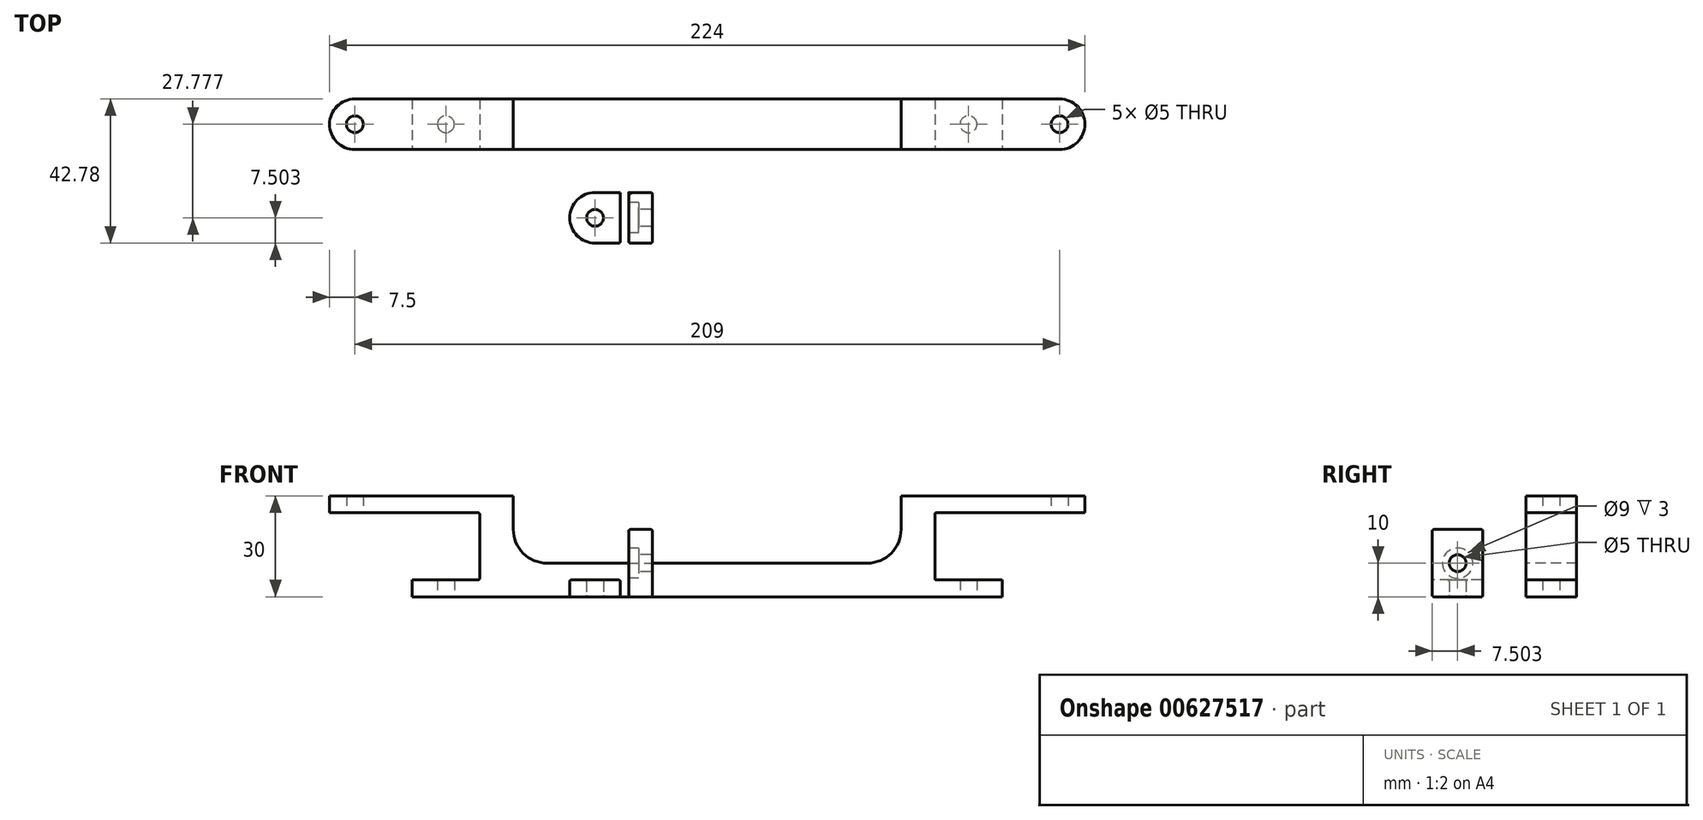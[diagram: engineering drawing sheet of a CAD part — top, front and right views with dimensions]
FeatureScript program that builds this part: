
annotation { "Feature Type Name" : "Feature", "Feature Type Description" : "" }
export const myFeature = defineFeature(function(context is Context, id is Id, definition is map)
    precondition{}
    {
        {
            var Q0;
            Q0=qCreatedBy(makeId("Top.planeOp"),FACE);
            var sketch = newSketch(context, id + "F0", { "sketchPlane" : qUnion([Q0])});
            skLineSegment(sketch, "E0", {"start": v(0, 0) * mm, "end": v(104.5, 0) * mm, "construction": true});
            skLineSegment(sketch, "E1", {"start": v(0, 0) * mm, "end": v(-104.5, 0) * mm, "construction": true});
            skCircle(sketch, "E2", {"center": v(-104.5, 0) * mm, "radius": 2.5 * mm});
            skCircle(sketch, "E3", {"center": v(104.5, 0) * mm, "radius": 2.5 * mm});
            skCircle(sketch, "E4.0", {"center": v(104.5, 0) * mm, "radius": 7.5 * mm});
            skCircle(sketch, "E5.0", {"center": v(-104.5, 0) * mm, "radius": 7.5 * mm});
            skLineSegment(sketch, "E6", {"start": v(104.5, 7.5) * mm, "end": v(-104.5, 7.5) * mm});
            skLineSegment(sketch, "E7", {"start": v(-104.5, -7.5) * mm, "end": v(104.5, -7.5) * mm});
            skSolve(sketch);
        }
        {
            var Q0;
            Q0=makeQuery(id+"F0.imprint","IMPRINT",FACE,{"disambiguationData":[TD([[makeQuery(id+"F0.imprint","IMPRINT",EDGE,{"derivedFrom":sQuery(id+"F0.wireOp",EDGE,"E2")}),-1.0]])]});
            var Q1;
            {var subQ0=sQuery(id+"F0.wireOp",EDGE,"E6");Q1=makeQuery(id+"F0.imprint","IMPRINT",FACE,{"disambiguationData":[TD([[makeQuery(id+"F0.imprint","IMPRINT",EDGE,{"derivedFrom":subQ0}),1.0]])]});}
            var Q2;
            Q2=makeQuery(id+"F0.imprint","IMPRINT",FACE,{"disambiguationData":[TD([[makeQuery(id+"F0.imprint","IMPRINT",EDGE,{"derivedFrom":sQuery(id+"F0.wireOp",EDGE,"E3")}),-1.0]])]});
            extrude(context, id + "F1", {"entities" : qUnion([Q0, Q1, Q2]), "depth" : 30 * mm, "offsetDistance" : 25 * mm});
        }
        {
            var Q0;
            Q0=makeQuery(id+"F1.opExtrude","SWEPT_FACE",FACE,{"disambiguationData":[OSD([sQuery(id+"F0.wireOp",EDGE,"E7")])]});
            var sketch = newSketch(context, id + "F2", { "sketchPlane" : qUnion([Q0])});
            skLineSegment(sketch, "E8", {"start": v(0, 0) * mm, "end": v(0, 30) * mm, "construction": true});
            skLineSegment(sketch, "E9.right", {"start": v(0, 0) * mm, "end": v(0, 20) * mm, "construction": true});
            skLineSegment(sketch, "E10.left", {"start": v(-67.5, 30) * mm, "end": v(-67.5, 0) * mm, "construction": true});
            skLineSegment(sketch, "E11.bottom", {"start": v(0, 30) * mm, "end": v(-57.5, 30) * mm});
            skLineSegment(sketch, "E11.top", {"start": v(0, 10) * mm, "end": v(-47.5, 10) * mm});
            skLineSegment(sketch, "E11.left", {"start": v(0, 30) * mm, "end": v(0, 10) * mm});
            skLineSegment(sketch, "E11.right", {"start": v(-57.5, 30) * mm, "end": v(-57.5, 20) * mm});
            skPoint(sketch, "E12.visualSharp", {"position": v(-57.5, 10) * mm});
            skArc(sketch, "E12.filletArc", {"start": v(-57.5, 20) * mm, "mid": v(-54.57, 12.93) * mm, "end": v(-47.5, 10) * mm});
            skLineSegment(sketch, "E13.MirrorCS", {"start": v(0, 10) * mm, "end": v(47.5, 10) * mm});
            skLineSegment(sketch, "E14.MirrorCS", {"start": v(0, 30) * mm, "end": v(57.5, 30) * mm});
            skLineSegment(sketch, "E15.MirrorCS", {"start": v(57.5, 30) * mm, "end": v(57.5, 20) * mm});
            skArc(sketch, "E16.MirrorCS", {"start": v(57.5, 20) * mm, "mid": v(54.57, 12.93) * mm, "end": v(47.5, 10) * mm});
            skLineSegment(sketch, "E17.bottom", {"start": v(-68, 25) * mm, "end": v(-118.82, 25) * mm});
            skLineSegment(sketch, "E17.top", {"start": v(-68, 5) * mm, "end": v(-87.5, 5) * mm});
            skLineSegment(sketch, "E17.left", {"start": v(-67.5, 24.5) * mm, "end": v(-67.5, 5.5) * mm});
            skLineSegment(sketch, "E17.right", {"start": v(-118.82, 25) * mm, "end": v(-118.82, 5) * mm});
            skPoint(sketch, "E18.visualSharp", {"position": v(-67.5, 25) * mm});
            skArc(sketch, "E18.filletArc", {"start": v(-67.5, 24.5) * mm, "mid": v(-67.65, 24.85) * mm, "end": v(-68, 25) * mm});
            skPoint(sketch, "E19.visualSharp", {"position": v(-67.5, 5) * mm});
            skArc(sketch, "E19.filletArc", {"start": v(-68, 5) * mm, "mid": v(-67.65, 5.15) * mm, "end": v(-67.5, 5.5) * mm});
            skLineSegment(sketch, "E20.MirrorCS", {"start": v(67.5, 24.5) * mm, "end": v(67.5, 5.5) * mm});
            skArc(sketch, "E21.MirrorCS", {"start": v(68, 5) * mm, "mid": v(67.65, 5.15) * mm, "end": v(67.5, 5.5) * mm});
            skLineSegment(sketch, "E22.MirrorCS", {"start": v(68, 5) * mm, "end": v(87.5, 5) * mm});
            skArc(sketch, "E23.MirrorCS", {"start": v(67.5, 24.5) * mm, "mid": v(67.65, 24.85) * mm, "end": v(68, 25) * mm});
            skLineSegment(sketch, "E24.MirrorCS", {"start": v(68, 25) * mm, "end": v(118.82, 25) * mm});
            skLineSegment(sketch, "E25.MirrorCS", {"start": v(118.82, 25) * mm, "end": v(118.82, 5) * mm});
            skLineSegment(sketch, "E26", {"start": v(-67.5, 0) * mm, "end": v(-87.5, 0) * mm, "construction": true});
            skLineSegment(sketch, "E27.bottom", {"start": v(-87.5, 0) * mm, "end": v(-118.82, 0) * mm});
            skLineSegment(sketch, "E27.left", {"start": v(-87.5, 0) * mm, "end": v(-87.5, 5) * mm});
            skLineSegment(sketch, "E27.right", {"start": v(-118.82, 0) * mm, "end": v(-118.82, 5) * mm});
            skLineSegment(sketch, "E28.MirrorCS", {"start": v(87.5, 0) * mm, "end": v(87.5, 5) * mm});
            skLineSegment(sketch, "E29.MirrorCS", {"start": v(118.82, 0) * mm, "end": v(118.82, 5) * mm});
            skLineSegment(sketch, "E30.MirrorCS", {"start": v(87.5, 0) * mm, "end": v(118.82, 0) * mm});
            skPoint(sketch, "E31.orphan", {"position": v(118.82, 5) * mm});
            skSolve(sketch);
        }
        {
            var Q0;
            Q0=makeQuery(id+"F2.imprint","IMPRINT",FACE,{"disambiguationData":[TD([[makeQuery(id+"F2.imprint","IMPRINT",EDGE,{"derivedFrom":sQuery(id+"F2.wireOp",EDGE,"E11.left")}),1.0]])]});
            var Q1;
            Q1=makeQuery(id+"F2.imprint","IMPRINT",FACE,{"disambiguationData":[TD([[makeQuery(id+"F2.imprint","IMPRINT",EDGE,{"derivedFrom":sQuery(id+"F2.wireOp",EDGE,"E11.bottom")}),-1.0]])]});
            var Q2;
            Q2=makeQuery(id+"F2.imprint","IMPRINT",FACE,{"disambiguationData":[TD([[makeQuery(id+"F2.imprint","IMPRINT",EDGE,{"derivedFrom":sQuery(id+"F2.wireOp",EDGE,"E20.MirrorCS")}),1.0]])]});
            var Q3;
            {var subQ4=sQuery(id+"F2.wireOp",EDGE,"E25.MirrorCS");Q3=makeQuery(id+"F2.imprint","IMPRINT",FACE,{"disambiguationData":[TD([[makeQuery(id+"F2.imprint","IMPRINT",EDGE,{"derivedFrom":subQ4}),-1.0]])]});}
            var Q4;
            Q4=makeQuery(id+"F2.imprint","IMPRINT",FACE,{"disambiguationData":[TD([[makeQuery(id+"F2.imprint","IMPRINT",EDGE,{"derivedFrom":sQuery(id+"F2.wireOp",EDGE,"E17.top")}),-1.0]])]});
            var Q5;
            {var subQ4=sQuery(id+"F2.wireOp",EDGE,"E17.right");Q5=makeQuery(id+"F2.imprint","IMPRINT",FACE,{"disambiguationData":[TD([[makeQuery(id+"F2.imprint","IMPRINT",EDGE,{"derivedFrom":subQ4}),1.0]])]});}
            extrude(context, id + "F3", {"entities" : qUnion([Q0, Q1, Q2, Q3, Q4, Q5]), "operationType" : NewBodyOperationType.REMOVE, "oppositeDirection" : true, "depth" : 25 * mm, "offsetDistance" : 25 * mm});
        }
        {
            var Q0;
            Q0=makeQuery(id+"F1.opExtrude","CAP_FACE",FACE,{"disambiguationData":[OSD([sQuery(id+"F0.wireOp",EDGE,"E2"),sQuery(id+"F0.wireOp",EDGE,"E3"),sQuery(id+"F0.wireOp",EDGE,"E4.0"),sQuery(id+"F0.wireOp",EDGE,"E5.0"),sQuery(id+"F0.wireOp",EDGE,"E6"),sQuery(id+"F0.wireOp",EDGE,"E7")])],"isStart":true});
            var sketch = newSketch(context, id + "F4", { "sketchPlane" : qUnion([Q0])});
            skCircle(sketch, "E32", {"center": v(-77.5, 0) * mm, "radius": 2.5 * mm});
            skCircle(sketch, "E33", {"center": v(77.5, 0) * mm, "radius": 2.5 * mm});
            skPoint(sketch, "E33.centerSnap0", {"position": v(87.5, 0) * mm});
            skSolve(sketch);
        }
        {
            var Q0;
            Q0=makeQuery(id+"F4.imprint","IMPRINT",FACE,{"disambiguationData":[TD([[makeQuery(id+"F4.imprint","IMPRINT",EDGE,{"derivedFrom":sQuery(id+"F4.wireOp",EDGE,"E32")}),1.0]])]});
            var Q1;
            Q1=makeQuery(id+"F4.imprint","IMPRINT",FACE,{"disambiguationData":[TD([[makeQuery(id+"F4.imprint","IMPRINT",EDGE,{"derivedFrom":sQuery(id+"F4.wireOp",EDGE,"E33")}),1.0]])]});
            extrude(context, id + "F5", {"entities" : qUnion([Q0, Q1]), "operationType" : NewBodyOperationType.REMOVE, "oppositeDirection" : true, "depth" : 25 * mm, "offsetDistance" : 25 * mm});
        }
        {
            var Q0;
            Q0=qCreatedBy(makeId("Top.planeOp"),FACE);
            var sketch = newSketch(context, id + "F6", { "sketchPlane" : qUnion([Q0])});
            skCircle(sketch, "E34", {"center": v(-33.27, -27.78) * mm, "radius": 2.5 * mm});
            skCircle(sketch, "E35.0", {"center": v(-33.27, -27.78) * mm, "radius": 7.5 * mm});
            skLineSegment(sketch, "E36", {"start": v(-33.27, -20.28) * mm, "end": v(-16.27, -20.28) * mm});
            skLineSegment(sketch, "E37", {"start": v(-16.27, -20.28) * mm, "end": v(-16.27, -35.28) * mm});
            skLineSegment(sketch, "E38", {"start": v(-16.27, -35.28) * mm, "end": v(-33.27, -35.28) * mm});
            skLineSegment(sketch, "E39", {"start": v(-25.77, -27.78) * mm, "end": v(-25.77, -20.28) * mm, "construction": true});
            skLineSegment(sketch, "E40", {"start": v(-25.77, -20.28) * mm, "end": v(-25.77, -35.28) * mm});
            skLineSegment(sketch, "E41.bottom", {"start": v(-25.77, -20.28) * mm, "end": v(-23.27, -20.28) * mm});
            skLineSegment(sketch, "E41.top", {"start": v(-25.77, -35.28) * mm, "end": v(-23.27, -35.28) * mm});
            skLineSegment(sketch, "E41.right", {"start": v(-23.27, -20.28) * mm, "end": v(-23.27, -35.28) * mm});
            skSolve(sketch);
        }
        {
            var Q0;
            {var subQ5=sQuery(id+"F6.wireOp",EDGE,"E37");Q0=makeQuery(id+"F6.imprint","IMPRINT",FACE,{"disambiguationData":[TD([[makeQuery(id+"F6.imprint","IMPRINT",EDGE,{"derivedFrom":subQ5}),-1.0]])]});}
            extrude(context, id + "F7", {"entities" : qUnion([Q0]), "depth" : 20 * mm, "offsetDistance" : 25 * mm});
        }
        {
            var Q0;
            Q0=makeQuery(id+"F6.imprint","IMPRINT",FACE,{"disambiguationData":[TD([[makeQuery(id+"F6.imprint","IMPRINT",EDGE,{"derivedFrom":sQuery(id+"F6.wireOp",EDGE,"E34")}),-1.0]])]});
            var Q1;
            {var subQ0=sQuery(id+"F6.wireOp",EDGE,"E38");var subQ1=sQuery(id+"F6.wireOp",EDGE,"E35.0");var subQ2=makeQuery(id+"F6.imprint","INTERSECT",VERTEX,{"derivedFrom":[subQ1,subQ0]});Q1=makeQuery(id+"F6.imprint","IMPRINT",FACE,{"disambiguationData":[TD([[makeQuery(id+"F6.imprint","IMPRINT",EDGE,{"disambiguationData":[TD([[subQ2,-1.0]])],"derivedFrom":subQ1}),-1.0]])]});}
            var Q2;
            {var subQ0=sQuery(id+"F6.wireOp",EDGE,"E36");var subQ1=sQuery(id+"F6.wireOp",EDGE,"E35.0");var subQ2=makeQuery(id+"F6.imprint","INTERSECT",VERTEX,{"derivedFrom":[subQ1,subQ0]});Q2=makeQuery(id+"F6.imprint","IMPRINT",FACE,{"disambiguationData":[TD([[makeQuery(id+"F6.imprint","IMPRINT",EDGE,{"disambiguationData":[TD([[subQ2,1.0]])],"derivedFrom":subQ1}),-1.0]])]});}
            var Q3;
            {var subQ3=sQuery(id+"F6.wireOp",EDGE,"E41.bottom");Q3=makeQuery(id+"F6.imprint","IMPRINT",FACE,{"disambiguationData":[TD([[makeQuery(id+"F6.imprint","IMPRINT",EDGE,{"derivedFrom":subQ3}),-1.0]])]});}
            extrude(context, id + "F8", {"entities" : qUnion([Q0, Q1, Q2, Q3]), "operationType" : NewBodyOperationType.ADD, "depth" : 5 * mm, "offsetDistance" : 25 * mm});
        }
        {
            var Q0;
            Q0=makeQuery(id+"F7.opExtrude","SWEPT_FACE",FACE,{"disambiguationData":[OSD([sQuery(id+"F6.wireOp",EDGE,"E41.right")])]});
            var sketch = newSketch(context, id + "F9", { "sketchPlane" : qUnion([Q0])});
            skCircle(sketch, "E42", {"center": v(27.78, 10) * mm, "radius": 2.5 * mm});
            skPoint(sketch, "E42.centerSnap0", {"position": v(27.78, 20) * mm});
            skCircle(sketch, "E43", {"center": v(27.78, 10) * mm, "radius": 4.5 * mm});
            skSolve(sketch);
        }
        {
            var Q0;
            Q0=makeQuery(id+"F9.imprint","IMPRINT",FACE,{"disambiguationData":[TD([[makeQuery(id+"F9.imprint","IMPRINT",EDGE,{"derivedFrom":sQuery(id+"F9.wireOp",EDGE,"E42")}),-1.0]])]});
            extrude(context, id + "F10", {"entities" : qUnion([Q0]), "operationType" : NewBodyOperationType.REMOVE, "oppositeDirection" : true, "depth" : 3 * mm, "offsetDistance" : 25 * mm});
        }
        {
            var Q0;
            Q0=makeQuery(id+"F10.boolean.opBoolean","SPLIT",FACE,{"disambiguationData":[TD([makeQuery(id+"F10.opExtrude","SWEPT_FACE",FACE,{"disambiguationData":[OSD([sQuery(id+"F9.wireOp",EDGE,"E42")])]})])],"derivedFrom":makeQuery(id+"F7.opExtrude","SWEPT_FACE",FACE,{"disambiguationData":[OSD([sQuery(id+"F6.wireOp",EDGE,"E41.right")])]})});
            extrude(context, id + "F11", {"entities" : qUnion([Q0]), "operationType" : NewBodyOperationType.REMOVE, "endBound" : BoundingType.UP_TO_NEXT, "oppositeDirection" : true, "depth" : 25 * mm, "offsetDistance" : 25 * mm});
        }
        {
            var Q0;
            Q0=makeQuery(id+"F7.opExtrude","CAP_FACE",FACE,{"disambiguationData":[OSD([sQuery(id+"F6.wireOp",EDGE,"E36"),sQuery(id+"F6.wireOp",EDGE,"E37"),sQuery(id+"F6.wireOp",EDGE,"E38"),sQuery(id+"F6.wireOp",EDGE,"E41.right")])],"isStart":false});
            var Q1;
            {var subQ0=sQuery(id+"F6.wireOp",EDGE,"E38");Q1=makeQuery(id+"F8.boolean.opBoolean","MERGE",FACE,{"derivedFrom":[makeQuery(id+"F7.opExtrude","SWEPT_FACE",FACE,{"disambiguationData":[OSD([subQ0])]}),makeQuery(id+"F8.opExtrude","SWEPT_FACE",FACE,{"disambiguationData":[OSD([subQ0,sQuery(id+"F6.wireOp",EDGE,"E41.top")])]})]});}
            var Q2;
            Q2=makeQuery(id+"F7.opExtrude","SWEPT_EDGE",EDGE,{"disambiguationData":[OSD([sQuery(id+"F6.wireOp",EDGE,"E36"),sQuery(id+"F6.wireOp",EDGE,"E37")])]});
            var Q3;
            Q3=makeQuery(id+"F8.opExtrude","CAP_FACE",FACE,{"disambiguationData":[OSD([sQuery(id+"F6.wireOp",EDGE,"E34"),sQuery(id+"F6.wireOp",EDGE,"E35.0"),sQuery(id+"F6.wireOp",EDGE,"E36"),sQuery(id+"F6.wireOp",EDGE,"E38"),sQuery(id+"F6.wireOp",EDGE,"E41.bottom"),sQuery(id+"F6.wireOp",EDGE,"E41.top"),sQuery(id+"F6.wireOp",EDGE,"E41.right")])],"isStart":false});
            var Q4;
            {var subQ0=sQuery(id+"F6.wireOp",EDGE,"E41.right");var subQ1=sQuery(id+"F6.wireOp",EDGE,"E38");var subQ2=sQuery(id+"F6.wireOp",EDGE,"E36");Q4=makeQuery(id+"F8.boolean.opBoolean","MERGE",FACE,{"derivedFrom":[makeQuery(id+"F7.opExtrude","CAP_FACE",FACE,{"disambiguationData":[OSD([subQ2,sQuery(id+"F6.wireOp",EDGE,"E37"),subQ1,subQ0])],"isStart":true}),makeQuery(id+"F8.opExtrude","CAP_FACE",FACE,{"disambiguationData":[OSD([sQuery(id+"F6.wireOp",EDGE,"E34"),sQuery(id+"F6.wireOp",EDGE,"E35.0"),subQ2,subQ1,sQuery(id+"F6.wireOp",EDGE,"E41.bottom"),sQuery(id+"F6.wireOp",EDGE,"E41.top"),subQ0])],"isStart":true})]});}
            var Q5;
            Q5=makeQuery(id+"F7.opExtrude","SWEPT_FACE",FACE,{"disambiguationData":[OSD([sQuery(id+"F6.wireOp",EDGE,"E37")])]});
            fillet(context, id + "F12", {"entities" : qUnion([Q0, Q1, Q2, Q3, Q4, Q5]), "radius" : 0.5 * mm, "tangentPropagation" : true, "allowEdgeOverflow" : false});
        }
    });
